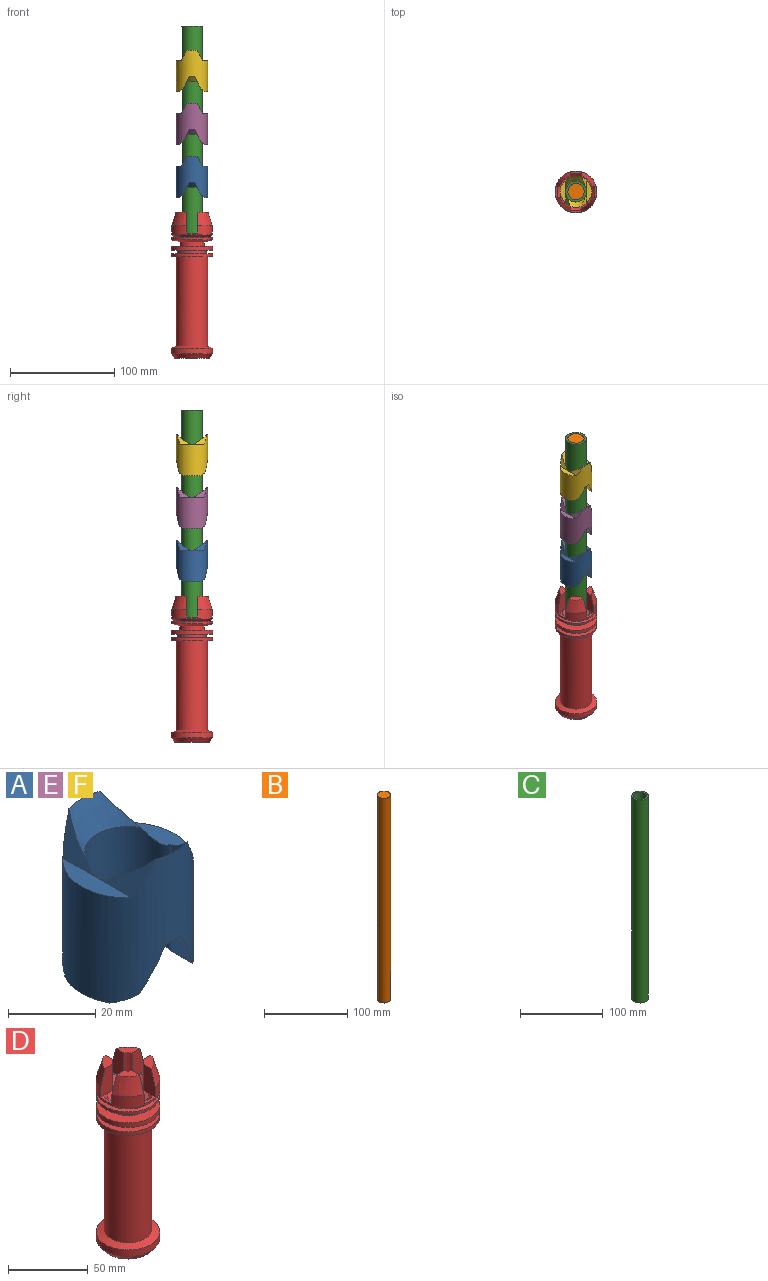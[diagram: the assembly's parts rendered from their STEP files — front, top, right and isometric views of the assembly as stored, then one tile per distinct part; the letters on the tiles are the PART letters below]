
ASSEMBLY  parts=6 mates=3
PART A: 20 faces, bbox 30x30x39.9 mm
  f0: cylinder r=10mm len=30.44mm, axis (0,0,-1), area 1619.7mm2, adj f5,f6,f8,f9,f10,f11,f12,f13
  f1: cylinder r=15mm len=39.88mm, axis (0,0,-1), area 2722.9mm2, adj f2,f3,f4,f5,f6,f7,f8,f9
  f2: plane 14.47x1.86mm, normal (0,0,-1), area 18.2mm2, adj f1,f16
  f3: plane 14.47x1.86mm, normal (0,0,-1), area 18.2mm2, adj f1,f17
  f4: plane 22.36x5mm, normal (0,0,1), area 77.4mm2, adj f1,f5,f6
  f5: plane 14.12x9.88mm, normal (-0.89,0,0.45), area 48.8mm2, adj f0,f1,f4,f15
  f6: plane 14.12x9.88mm, normal (-0.89,0,0.45), area 48.8mm2, adj f0,f1,f4,f14
  f7: plane 22.36x5mm, normal (0,0,1), area 77.4mm2, adj f1,f8,f9
  f8: plane 14.12x9.88mm, normal (0.89,0,0.45), area 48.8mm2, adj f0,f1,f7,f14
  f9: plane 14.12x9.88mm, normal (0.89,0,0.45), area 48.8mm2, adj f0,f1,f7,f15
  f10: plane 12.27x9.69mm, normal (-0.89,0,-0.45), area 64.5mm2, adj f0,f1,f16,f19
  f11: plane 12.27x9.69mm, normal (0.89,0,-0.45), area 64.5mm2, adj f0,f1,f17,f19
  f12: plane 12.27x9.69mm, normal (0.89,0,-0.45), area 64.5mm2, adj f0,f1,f17,f18
  f13: plane 12.27x9.69mm, normal (-0.89,0,-0.45), area 64.5mm2, adj f0,f1,f16,f18
  f14: cone r=10mm half-angle=33.7deg, axis (0,0,1), area 135.6mm2, adj f0,f1,f6,f8
  f15: cone r=10mm half-angle=33.7deg, axis (0,0,1), area 135.6mm2, adj f0,f1,f5,f9
  f16: plane 24.59x4.54mm, normal (-0.53,0,-0.85), area 97.1mm2, adj f0,f1,f2,f10,f13
  f17: plane 24.59x4.54mm, normal (0.53,0,-0.85), area 97.1mm2, adj f0,f1,f3,f11,f12
  f18: cone r=9.92mm half-angle=45deg, axis (0,0,1), area 53.6mm2, adj f0,f1,f12,f13
  f19: cone r=9.92mm half-angle=45deg, axis (0,0,1), area 53.6mm2, adj f0,f1,f10,f11
PART B: 3 faces, bbox 15.6x15.6x300 mm
  f0: cylinder r=7.8mm len=300mm, axis (0,0,-1), area 14702.7mm2, adj f1,f2
  f1: plane 15.6x15.6mm, normal (0,0,1), area 191.1mm2, adj f0
  f2: plane 15.6x15.6mm, normal (0,0,-1), area 191.1mm2, adj f0
PART C: 4 faces, bbox 20x20x300 mm
  f0: cylinder r=7.8mm len=300mm, axis (0,0,-1), area 14702.7mm2, adj f2,f3
  f1: cylinder r=10mm len=300mm, axis (0,0,-1), area 18849.6mm2, adj f2,f3
  f2: plane 20x20mm, normal (0,0,1), area 123mm2, adj f0,f1
  f3: plane 20x20mm, normal (0,0,-1), area 123mm2, adj f0,f1
PART D: 79 faces, bbox 40.1x40.1x140.1 mm
  f0: plane 10x2.71mm, normal (0,0,1), area 20.2mm2, adj f3,f5,f19,f48
  f1: plane 10x2.71mm, normal (0,0,1), area 20.2mm2, adj f3,f6,f9,f48
  f2: plane 10x2.71mm, normal (0,0,1), area 20.2mm2, adj f3,f10,f13,f48
  f3: cylinder r=20mm len=40mm, axis (0,0,-1), area 814.4mm2, adj f0,f1,f2,f4,f5,f6,f9,f10
  f4: plane 10x2.71mm, normal (0,0,1), area 20.2mm2, adj f3,f14,f18,f48
  f5: plane 20.12x10.83mm, normal (0,-1,0), area 189mm2, adj f0,f3,f7,f8,f22,f42
  f6: plane 20.12x10.83mm, normal (-1,0,0), area 189mm2, adj f1,f3,f7,f8,f22,f42
  f7: cylinder r=10mm len=20mm, axis (0,0,-1), area 104.7mm2, adj f5,f6,f8,f42
  f8: plane 10.4x10.4mm, normal (0,0,1), area 63.7mm2, adj f5,f6,f7,f22
  f9: plane 20.12x10.83mm, normal (1,0,0), area 189mm2, adj f1,f3,f11,f12,f23,f43
  f10: plane 20.12x10.83mm, normal (0,-1,0), area 189mm2, adj f2,f3,f11,f12,f23,f43
  f11: cylinder r=10mm len=20mm, axis (0,0,-1), area 104.7mm2, adj f9,f10,f12,f43
  f12: plane 10.4x10.4mm, normal (0,0,1), area 63.7mm2, adj f9,f10,f11,f23
  f13: plane 20.12x10.83mm, normal (0,1,0), area 189mm2, adj f2,f3,f15,f16,f24,f49
  f14: plane 20.12x10.83mm, normal (1,0,0), area 189mm2, adj f3,f4,f15,f16,f24,f49
  f15: cylinder r=10mm len=20mm, axis (0,0,-1), area 104.7mm2, adj f13,f14,f16,f49
  f16: plane 10.4x10.4mm, normal (0,0,1), area 63.7mm2, adj f13,f14,f15,f24
  f17: cylinder r=10mm len=20mm, axis (0,0,-1), area 104.7mm2, adj f18,f19,f20,f44
  f18: plane 20.12x10.83mm, normal (-1,0,0), area 189mm2, adj f3,f4,f17,f20,f21,f44
  f19: plane 20.12x10.83mm, normal (0,1,0), area 189mm2, adj f0,f3,f17,f20,f21,f44
  f20: plane 10.4x10.4mm, normal (0,0,1), area 63.7mm2, adj f17,f18,f19,f21
  f21: cone r=16.19mm half-angle=16.7deg, axis (0,0,-1), area 241.4mm2, adj f3,f18,f19,f20
  f22: cone r=16.19mm half-angle=16.7deg, axis (0,0,-1), area 241.4mm2, adj f3,f5,f6,f8
  f23: cone r=16.19mm half-angle=16.7deg, axis (0,0,-1), area 241.4mm2, adj f3,f9,f10,f12
  f24: cone r=16.19mm half-angle=16.7deg, axis (0,0,-1), area 241.4mm2, adj f3,f13,f14,f16
  f25: cone r=17.35mm half-angle=46.5deg, axis (0,0,1), area 428.6mm2, adj f3,f26
  f26: cone r=25.13mm half-angle=80.5deg, axis (0,0,-1), area 315.1mm2, adj f25,f27
  f27: cylinder r=20mm len=40mm, axis (0,0,-1), area 261.9mm2, adj f26,f28
  f28: cone r=12mm half-angle=76.5deg, axis (0,0,1), area 827mm2, adj f27,f29
  f29: cylinder r=12mm len=24mm, axis (0,0,1), area 334.2mm2, adj f28,f30
  f30: plane 40x40mm, normal (0,0,1), area 804.2mm2, adj f29,f31
  f31: cylinder r=20mm len=40mm, axis (0,0,-1), area 445.6mm2, adj f30,f32
  f32: plane 40x40mm, normal (0,0,-1), area 669.6mm2, adj f31,f33
  f33: cylinder r=13.67mm len=27.34mm, axis (0,0,1), area 279.2mm2, adj f32,f34
  f34: plane 40x40mm, normal (0,0,1), area 669.6mm2, adj f33,f35
  f35: cylinder r=20mm len=40mm, axis (0,0,-1), area 370.8mm2, adj f34,f36
  f36: plane 40x40mm, normal (0,0,-1), area 549.8mm2, adj f35,f37
  f37: cylinder r=15mm len=86.17mm, axis (0,0,1), area 8121mm2, adj f36,f38
  f38: cone r=23.07mm half-angle=68.7deg, axis (0,0,-1), area 590.2mm2, adj f37,f39
  f39: cylinder r=20mm len=40mm, axis (0,0,-1), area 639mm2, adj f38,f40
  f40: cone r=15mm half-angle=38.3deg, axis (0,0,1), area 606.9mm2, adj f39,f41
  f41: plane 33.49x33.49mm, normal (0,0,-1), area 880.8mm2, adj f40
  f42: plane 12.29x12.29mm, normal (0,0,-1), area 40.1mm2, adj f5,f6,f7,f48,f50,f51,f52
  f43: plane 12.29x12.29mm, normal (0,0,-1), area 40.1mm2, adj f9,f10,f11,f48,f54,f55,f56
  f44: plane 12.29x12.29mm, normal (0,0,-1), area 40.1mm2, adj f17,f18,f19,f48,f62,f63,f64
  f45: plane 26x26mm, normal (0,0,-1), area 103.1mm2, adj f73,f74
  f46: plane 23.34x23.34mm, normal (0,0,-1), area 113.6mm2, adj f72,f73
  f47: cone r=24.8mm half-angle=80.5deg, axis (0,0,-1), area 180.3mm2, adj f70,f71
  f48: cylinder r=18mm len=36mm, axis (0,0,-1), area 465.3mm2, adj f0,f1,f2,f4,f42,f43,f44,f49
  f49: plane 12.29x12.29mm, normal (0,0,-1), area 40.1mm2, adj f13,f14,f15,f48,f58,f59,f60
  f50: plane 18x6.84mm, normal (0,1,0), area 103.1mm2, adj f42,f48,f52,f53,f67
  f51: plane 18x6.84mm, normal (1,0,0), area 103.1mm2, adj f42,f48,f52,f53,f67
  f52: cylinder r=12mm len=18mm, axis (0,0,-1), area 70.2mm2, adj f42,f50,f51,f53
  f53: plane 5.93x5.93mm, normal (0,0,-1), area 16.8mm2, adj f50,f51,f52,f67
  f54: plane 18x6.84mm, normal (-1,0,0), area 103.1mm2, adj f43,f48,f56,f57,f68
  f55: plane 18x6.84mm, normal (0,1,0), area 103.1mm2, adj f43,f48,f56,f57,f68
  f56: cylinder r=12mm len=18mm, axis (0,0,-1), area 70.2mm2, adj f43,f54,f55,f57
  f57: plane 5.93x5.93mm, normal (0,0,-1), area 16.8mm2, adj f54,f55,f56,f68
  f58: plane 18x6.84mm, normal (0,-1,0), area 103.1mm2, adj f48,f49,f60,f61,f69
  f59: plane 18x6.84mm, normal (-1,0,0), area 103.1mm2, adj f48,f49,f60,f61,f69
  f60: cylinder r=12mm len=18mm, axis (0,0,-1), area 70.2mm2, adj f49,f58,f59,f61
  f61: plane 5.93x5.93mm, normal (0,0,-1), area 16.8mm2, adj f58,f59,f60,f69
  f62: cylinder r=12mm len=18mm, axis (0,0,-1), area 70.2mm2, adj f44,f63,f64,f65
  f63: plane 18x6.84mm, normal (1,0,0), area 103.1mm2, adj f44,f48,f62,f65,f66
  f64: plane 18x6.84mm, normal (0,-1,0), area 103.1mm2, adj f44,f48,f62,f65,f66
  f65: plane 5.93x5.93mm, normal (0,0,-1), area 16.8mm2, adj f62,f63,f64,f66
  f66: cone r=14.27mm half-angle=16.7deg, axis (0,0,-1), area 128.7mm2, adj f48,f63,f64,f65
  f67: cone r=14.27mm half-angle=16.7deg, axis (0,0,-1), area 128.7mm2, adj f48,f50,f51,f53
  f68: cone r=14.27mm half-angle=16.7deg, axis (0,0,-1), area 128.7mm2, adj f48,f54,f55,f57
  f69: cone r=14.27mm half-angle=16.7deg, axis (0,0,-1), area 128.7mm2, adj f48,f58,f59,f61
  f70: cone r=15.97mm half-angle=46.5deg, axis (0,0,1), area 664.3mm2, adj f47,f48
  f71: cone r=11.53mm half-angle=76.5deg, axis (0,0,1), area 411.3mm2, adj f47,f72
  f72: cylinder r=10mm len=20mm, axis (0,0,1), area 503.3mm2, adj f46,f71
  f73: cylinder r=11.67mm len=23.34mm, axis (0,0,1), area 498.4mm2, adj f45,f46
  f74: cylinder r=13mm len=88.48mm, axis (0,0,1), area 7227.5mm2, adj f45,f75
  f75: cone r=22.34mm half-angle=68.7deg, axis (0,0,-1), area 522.7mm2, adj f74,f76
  f76: cylinder r=18mm len=36mm, axis (0,0,-1), area 342.1mm2, adj f75,f77
  f77: cone r=13.43mm half-angle=38.3deg, axis (0,0,1), area 381.4mm2, adj f76,f78
  f78: plane 31.55x31.55mm, normal (0,0,1), area 781.8mm2, adj f77
PART E: same geometry as A
PART F: same geometry as A
PLACE A t=(75.34,51.17,129.87)mm
PLACE B t=(9.74,88.73,-5.23)mm
PLACE C t=(-32.95,51.17,-5.23)mm
PLACE D t=(-90.71,51.17,-24.03)mm fixed
PLACE E t=(75.34,51.17,180.67)mm
PLACE F t=(75.34,51.17,231.47)mm
MATE slider C.f1 <-> D.f3  axis (0,0,-1) through (-32.95,51.17,-5.23)mm
MATE fastened B.f0 <-> C.f1  axis (0,0,1) through (-32.95,51.17,294.77)mm
MATE slider A.f0 <-> C.f1  axis (0,0,-1) through (-32.95,51.17,162.25)mm
